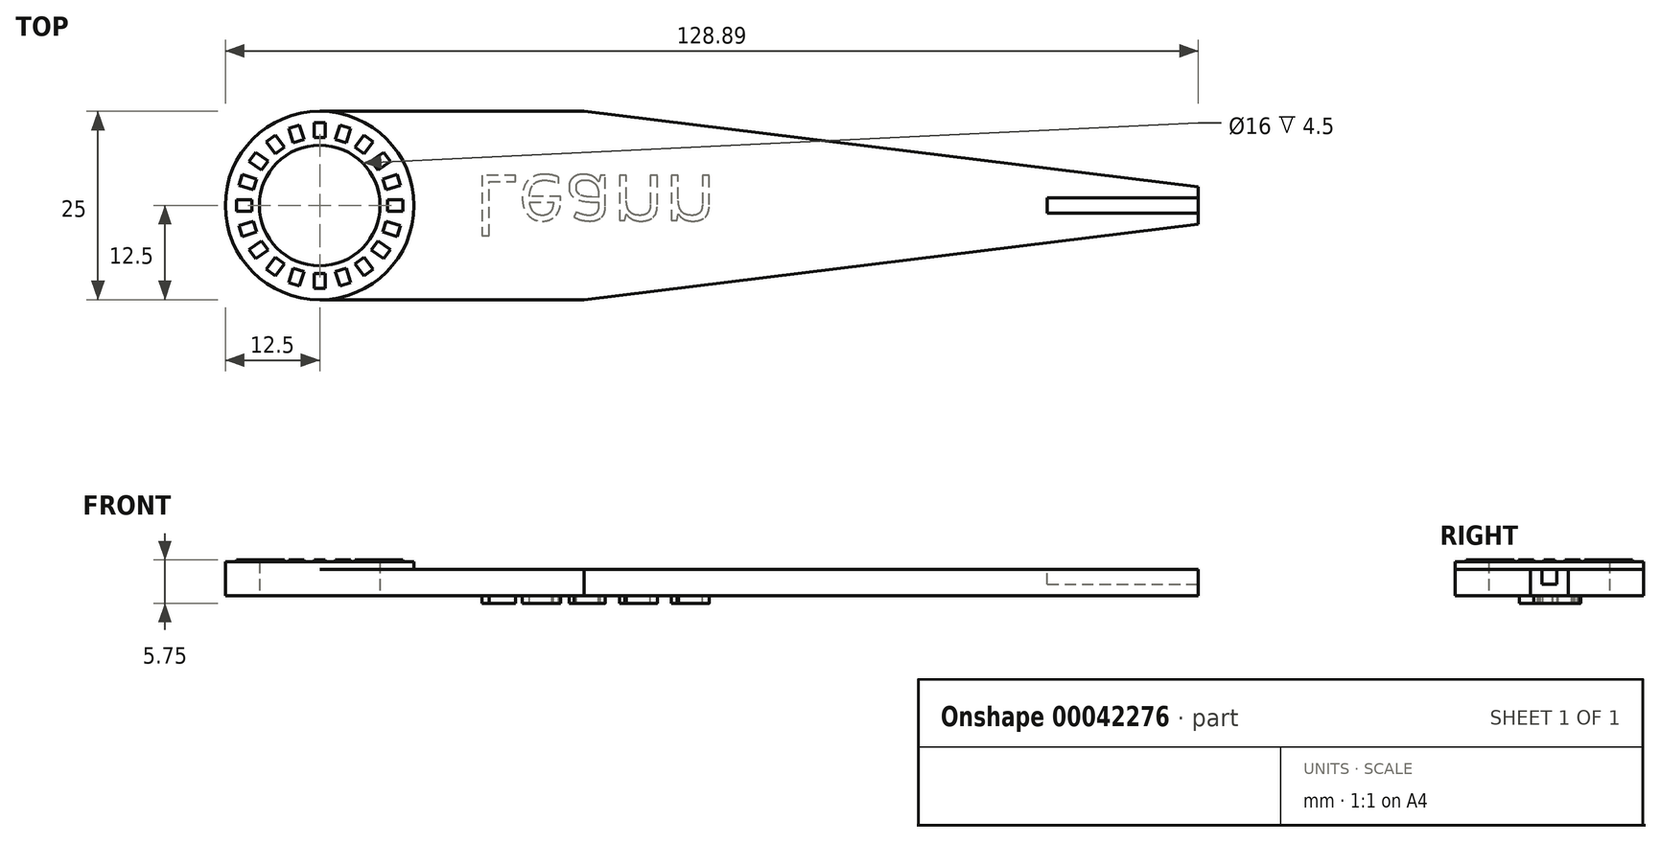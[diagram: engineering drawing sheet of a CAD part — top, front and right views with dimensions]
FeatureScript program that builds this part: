
annotation { "Feature Type Name" : "Feature", "Feature Type Description" : "" }
export const myFeature = defineFeature(function(context is Context, id is Id, definition is map)
    precondition{}
    {
        {
            var Q0;
            Q0=qCreatedBy(makeId("Top.planeOp"),FACE);
            var sketch = newSketch(context, id + "F0", { "sketchPlane" : qUnion([Q0])});
            skCircle(sketch, "E0", {"center": v(0, 0) * mm, "radius": 8 * mm});
            skArc(sketch, "E1", {"start": v(0, 12.5) * mm, "mid": v(-12.5, 0) * mm, "end": v(0, -12.5) * mm});
            skLineSegment(sketch, "E2", {"start": v(0, 12.5) * mm, "end": v(35, 12.5) * mm});
            skLineSegment(sketch, "E3", {"start": v(35, 12.5) * mm, "end": v(116.39, 2.5) * mm});
            skLineSegment(sketch, "E4", {"start": v(35, 12.5) * mm, "end": v(79.82, 12.5) * mm, "construction": true});
            skLineSegment(sketch, "E5", {"start": v(0, 0) * mm, "end": v(36.3, 0) * mm, "construction": true});
            skLineSegment(sketch, "E6.MirrorCS", {"start": v(0, -12.5) * mm, "end": v(35, -12.5) * mm});
            skLineSegment(sketch, "E7.MirrorCS", {"start": v(35, -12.5) * mm, "end": v(116.39, -2.5) * mm});
            skLineSegment(sketch, "E8", {"start": v(116.39, 2.5) * mm, "end": v(116.39, -2.5) * mm});
            skSolve(sketch);
        }
        {
            var Q0;
            Q0 = qSketchRegion(id + "F0", true);
            extrude(context, id + "F1", {"entities" : qUnion([Q0]), "depth" : 3.5 * mm});
        }
        {
            var Q0;
            Q0=makeQuery(id+"F1.opExtrude","CAP_FACE",FACE,{"disambiguationData":[OSD([sQuery(id+"F0.wireOp",EDGE,"E0"),sQuery(id+"F0.wireOp",EDGE,"E1"),sQuery(id+"F0.wireOp",EDGE,"E2"),sQuery(id+"F0.wireOp",EDGE,"E3"),sQuery(id+"F0.wireOp",EDGE,"E6.MirrorCS"),sQuery(id+"F0.wireOp",EDGE,"E7.MirrorCS"),sQuery(id+"F0.wireOp",EDGE,"E8")])],"isStart":false});
            var sketch = newSketch(context, id + "F2", { "sketchPlane" : qUnion([Q0])});
            skCircle(sketch, "E9", {"center": v(0, 0) * mm, "radius": 8 * mm});
            skCircle(sketch, "E10", {"center": v(0, 0) * mm, "radius": 12.5 * mm});
            skSolve(sketch);
        }
        {
            var Q0;
            Q0 = qSketchRegion(id + "F2", true);
            extrude(context, id + "F3", {"entities" : qUnion([Q0]), "operationType" : NewBodyOperationType.ADD, "depth" : 1 * mm});
        }
        {
            var Q0;
            Q0=makeQuery(id+"F3.opExtrude","CAP_FACE",FACE,{"disambiguationData":[OSD([sQuery(id+"F2.wireOp",EDGE,"E9"),sQuery(id+"F2.wireOp",EDGE,"E10")])],"isStart":false});
            var sketch = newSketch(context, id + "F4", { "sketchPlane" : qUnion([Q0])});
            skLineSegment(sketch, "E11.bottom", {"start": v(-0.75, 11) * mm, "end": v(0.75, 11) * mm});
            skLineSegment(sketch, "E11.top", {"start": v(-0.75, 9) * mm, "end": v(0.75, 9) * mm});
            skLineSegment(sketch, "E11.left", {"start": v(-0.75, 11) * mm, "end": v(-0.75, 9) * mm});
            skLineSegment(sketch, "E11.right", {"start": v(0.75, 11) * mm, "end": v(0.75, 9) * mm});
            skPoint(sketch, "E12", {"position": v(0, 8) * mm});
            skLineSegment(sketch, "E13.1.0", {"start": v(-4.11, 10.23) * mm, "end": v(-2.69, 10.7) * mm});
            skLineSegment(sketch, "E13.1.1", {"start": v(-4.11, 10.23) * mm, "end": v(-3.5, 8.33) * mm});
            skLineSegment(sketch, "E13.1.2", {"start": v(-3.5, 8.33) * mm, "end": v(-2.07, 8.8) * mm});
            skLineSegment(sketch, "E13.1.3", {"start": v(-2.69, 10.7) * mm, "end": v(-2.07, 8.8) * mm});
            skLineSegment(sketch, "E13.2.0", {"start": v(-7.07, 8.46) * mm, "end": v(-5.86, 9.34) * mm});
            skLineSegment(sketch, "E13.2.1", {"start": v(-7.07, 8.46) * mm, "end": v(-5.9, 6.84) * mm});
            skLineSegment(sketch, "E13.2.2", {"start": v(-5.9, 6.84) * mm, "end": v(-4.68, 7.72) * mm});
            skLineSegment(sketch, "E13.2.3", {"start": v(-5.86, 9.34) * mm, "end": v(-4.68, 7.72) * mm});
            skLineSegment(sketch, "E13.3.0", {"start": v(-9.34, 5.86) * mm, "end": v(-8.46, 7.07) * mm});
            skLineSegment(sketch, "E13.3.1", {"start": v(-9.34, 5.86) * mm, "end": v(-7.72, 4.68) * mm});
            skLineSegment(sketch, "E13.3.2", {"start": v(-7.72, 4.68) * mm, "end": v(-6.84, 5.9) * mm});
            skLineSegment(sketch, "E13.3.3", {"start": v(-8.46, 7.07) * mm, "end": v(-6.84, 5.9) * mm});
            skLineSegment(sketch, "E13.4.0", {"start": v(-10.7, 2.69) * mm, "end": v(-10.23, 4.11) * mm});
            skLineSegment(sketch, "E13.4.1", {"start": v(-10.7, 2.69) * mm, "end": v(-8.8, 2.07) * mm});
            skLineSegment(sketch, "E13.4.2", {"start": v(-8.8, 2.07) * mm, "end": v(-8.33, 3.5) * mm});
            skLineSegment(sketch, "E13.4.3", {"start": v(-10.23, 4.11) * mm, "end": v(-8.33, 3.5) * mm});
            skLineSegment(sketch, "E13.5.0", {"start": v(-11, -0.75) * mm, "end": v(-11, 0.75) * mm});
            skLineSegment(sketch, "E13.5.1", {"start": v(-11, -0.75) * mm, "end": v(-9, -0.75) * mm});
            skLineSegment(sketch, "E13.5.2", {"start": v(-9, -0.75) * mm, "end": v(-9, 0.75) * mm});
            skLineSegment(sketch, "E13.5.3", {"start": v(-11, 0.75) * mm, "end": v(-9, 0.75) * mm});
            skLineSegment(sketch, "E13.6.0", {"start": v(-10.23, -4.11) * mm, "end": v(-10.7, -2.69) * mm});
            skLineSegment(sketch, "E13.6.1", {"start": v(-10.23, -4.11) * mm, "end": v(-8.33, -3.5) * mm});
            skLineSegment(sketch, "E13.6.2", {"start": v(-8.33, -3.5) * mm, "end": v(-8.8, -2.07) * mm});
            skLineSegment(sketch, "E13.6.3", {"start": v(-10.7, -2.69) * mm, "end": v(-8.8, -2.07) * mm});
            skLineSegment(sketch, "E13.7.0", {"start": v(-8.46, -7.07) * mm, "end": v(-9.34, -5.86) * mm});
            skLineSegment(sketch, "E13.7.1", {"start": v(-8.46, -7.07) * mm, "end": v(-6.84, -5.9) * mm});
            skLineSegment(sketch, "E13.7.2", {"start": v(-6.84, -5.9) * mm, "end": v(-7.72, -4.68) * mm});
            skLineSegment(sketch, "E13.7.3", {"start": v(-9.34, -5.86) * mm, "end": v(-7.72, -4.68) * mm});
            skLineSegment(sketch, "E13.8.0", {"start": v(-5.86, -9.34) * mm, "end": v(-7.07, -8.46) * mm});
            skLineSegment(sketch, "E13.8.1", {"start": v(-5.86, -9.34) * mm, "end": v(-4.68, -7.72) * mm});
            skLineSegment(sketch, "E13.8.2", {"start": v(-4.68, -7.72) * mm, "end": v(-5.9, -6.84) * mm});
            skLineSegment(sketch, "E13.8.3", {"start": v(-7.07, -8.46) * mm, "end": v(-5.9, -6.84) * mm});
            skLineSegment(sketch, "E13.9.0", {"start": v(-2.69, -10.7) * mm, "end": v(-4.11, -10.23) * mm});
            skLineSegment(sketch, "E13.9.1", {"start": v(-2.69, -10.7) * mm, "end": v(-2.07, -8.8) * mm});
            skLineSegment(sketch, "E13.9.2", {"start": v(-2.07, -8.8) * mm, "end": v(-3.5, -8.33) * mm});
            skLineSegment(sketch, "E13.9.3", {"start": v(-4.11, -10.23) * mm, "end": v(-3.5, -8.33) * mm});
            skLineSegment(sketch, "E13.10.0", {"start": v(0.75, -11) * mm, "end": v(-0.75, -11) * mm});
            skLineSegment(sketch, "E13.10.1", {"start": v(0.75, -11) * mm, "end": v(0.75, -9) * mm});
            skLineSegment(sketch, "E13.10.2", {"start": v(0.75, -9) * mm, "end": v(-0.75, -9) * mm});
            skLineSegment(sketch, "E13.10.3", {"start": v(-0.75, -11) * mm, "end": v(-0.75, -9) * mm});
            skLineSegment(sketch, "E13.11.0", {"start": v(4.11, -10.23) * mm, "end": v(2.69, -10.7) * mm});
            skLineSegment(sketch, "E13.11.1", {"start": v(4.11, -10.23) * mm, "end": v(3.5, -8.33) * mm});
            skLineSegment(sketch, "E13.11.2", {"start": v(3.5, -8.33) * mm, "end": v(2.07, -8.8) * mm});
            skLineSegment(sketch, "E13.11.3", {"start": v(2.69, -10.7) * mm, "end": v(2.07, -8.8) * mm});
            skLineSegment(sketch, "E13.12.0", {"start": v(7.07, -8.46) * mm, "end": v(5.86, -9.34) * mm});
            skLineSegment(sketch, "E13.12.1", {"start": v(7.07, -8.46) * mm, "end": v(5.9, -6.84) * mm});
            skLineSegment(sketch, "E13.12.2", {"start": v(5.9, -6.84) * mm, "end": v(4.68, -7.72) * mm});
            skLineSegment(sketch, "E13.12.3", {"start": v(5.86, -9.34) * mm, "end": v(4.68, -7.72) * mm});
            skLineSegment(sketch, "E13.13.0", {"start": v(9.34, -5.86) * mm, "end": v(8.46, -7.07) * mm});
            skLineSegment(sketch, "E13.13.1", {"start": v(9.34, -5.86) * mm, "end": v(7.72, -4.68) * mm});
            skLineSegment(sketch, "E13.13.2", {"start": v(7.72, -4.68) * mm, "end": v(6.84, -5.9) * mm});
            skLineSegment(sketch, "E13.13.3", {"start": v(8.46, -7.07) * mm, "end": v(6.84, -5.9) * mm});
            skLineSegment(sketch, "E13.14.0", {"start": v(10.7, -2.69) * mm, "end": v(10.23, -4.11) * mm});
            skLineSegment(sketch, "E13.14.1", {"start": v(10.7, -2.69) * mm, "end": v(8.8, -2.07) * mm});
            skLineSegment(sketch, "E13.14.2", {"start": v(8.8, -2.07) * mm, "end": v(8.33, -3.5) * mm});
            skLineSegment(sketch, "E13.14.3", {"start": v(10.23, -4.11) * mm, "end": v(8.33, -3.5) * mm});
            skLineSegment(sketch, "E13.15.0", {"start": v(11, 0.75) * mm, "end": v(11, -0.75) * mm});
            skLineSegment(sketch, "E13.15.1", {"start": v(11, 0.75) * mm, "end": v(9, 0.75) * mm});
            skLineSegment(sketch, "E13.15.2", {"start": v(9, 0.75) * mm, "end": v(9, -0.75) * mm});
            skLineSegment(sketch, "E13.15.3", {"start": v(11, -0.75) * mm, "end": v(9, -0.75) * mm});
            skLineSegment(sketch, "E13.16.0", {"start": v(10.23, 4.11) * mm, "end": v(10.7, 2.69) * mm});
            skLineSegment(sketch, "E13.16.1", {"start": v(10.23, 4.11) * mm, "end": v(8.33, 3.5) * mm});
            skLineSegment(sketch, "E13.16.2", {"start": v(8.33, 3.5) * mm, "end": v(8.8, 2.07) * mm});
            skLineSegment(sketch, "E13.16.3", {"start": v(10.7, 2.69) * mm, "end": v(8.8, 2.07) * mm});
            skLineSegment(sketch, "E13.17.0", {"start": v(8.46, 7.07) * mm, "end": v(9.34, 5.86) * mm});
            skLineSegment(sketch, "E13.17.1", {"start": v(8.46, 7.07) * mm, "end": v(6.84, 5.9) * mm});
            skLineSegment(sketch, "E13.17.2", {"start": v(6.84, 5.9) * mm, "end": v(7.72, 4.68) * mm});
            skLineSegment(sketch, "E13.17.3", {"start": v(9.34, 5.86) * mm, "end": v(7.72, 4.68) * mm});
            skLineSegment(sketch, "E13.18.0", {"start": v(5.86, 9.34) * mm, "end": v(7.07, 8.46) * mm});
            skLineSegment(sketch, "E13.18.1", {"start": v(5.86, 9.34) * mm, "end": v(4.68, 7.72) * mm});
            skLineSegment(sketch, "E13.18.2", {"start": v(4.68, 7.72) * mm, "end": v(5.9, 6.84) * mm});
            skLineSegment(sketch, "E13.18.3", {"start": v(7.07, 8.46) * mm, "end": v(5.9, 6.84) * mm});
            skLineSegment(sketch, "E13.19.0", {"start": v(2.69, 10.7) * mm, "end": v(4.11, 10.23) * mm});
            skLineSegment(sketch, "E13.19.1", {"start": v(2.69, 10.7) * mm, "end": v(2.07, 8.8) * mm});
            skLineSegment(sketch, "E13.19.2", {"start": v(2.07, 8.8) * mm, "end": v(3.5, 8.33) * mm});
            skLineSegment(sketch, "E13.19.3", {"start": v(4.11, 10.23) * mm, "end": v(3.5, 8.33) * mm});
            skPoint(sketch, "E13.center", {"position": v(0, 0) * mm});
            skSolve(sketch);
        }
        {
            var Q0;
            Q0 = qSketchRegion(id + "F4", true);
            extrude(context, id + "F5", {"entities" : qUnion([Q0]), "operationType" : NewBodyOperationType.ADD, "depth" : .25 * mm});
        }
        {
            var Q0;
            Q0=makeQuery(id+"F1.opExtrude","CAP_FACE",FACE,{"disambiguationData":[OSD([sQuery(id+"F0.wireOp",EDGE,"E0"),sQuery(id+"F0.wireOp",EDGE,"E1"),sQuery(id+"F0.wireOp",EDGE,"E2"),sQuery(id+"F0.wireOp",EDGE,"E3"),sQuery(id+"F0.wireOp",EDGE,"E6.MirrorCS"),sQuery(id+"F0.wireOp",EDGE,"E7.MirrorCS"),sQuery(id+"F0.wireOp",EDGE,"E8")])],"isStart":false});
            var sketch = newSketch(context, id + "F6", { "sketchPlane" : qUnion([Q0])});
            skLineSegment(sketch, "E14.bottom", {"start": v(96.39, 1) * mm, "end": v(116.39, 1) * mm});
            skLineSegment(sketch, "E14.top", {"start": v(96.39, -1) * mm, "end": v(116.39, -1) * mm});
            skLineSegment(sketch, "E14.left", {"start": v(96.39, 1) * mm, "end": v(96.39, -1) * mm});
            skLineSegment(sketch, "E14.right", {"start": v(116.39, 1) * mm, "end": v(116.39, -1) * mm});
            skSolve(sketch);
        }
        {
            var Q0;
            Q0 = qSketchRegion(id + "F6", true);
            extrude(context, id + "F7", {"entities" : qUnion([Q0]), "operationType" : NewBodyOperationType.REMOVE, "oppositeDirection" : true, "depth" : 2 * mm});
        }
        {
            var Q0;
            Q0=makeQuery(id+"F1.opExtrude","CAP_FACE",FACE,{"disambiguationData":[OSD([sQuery(id+"F0.wireOp",EDGE,"E0"),sQuery(id+"F0.wireOp",EDGE,"E1"),sQuery(id+"F0.wireOp",EDGE,"E2"),sQuery(id+"F0.wireOp",EDGE,"E3"),sQuery(id+"F0.wireOp",EDGE,"E6.MirrorCS"),sQuery(id+"F0.wireOp",EDGE,"E7.MirrorCS"),sQuery(id+"F0.wireOp",EDGE,"E8")])],"isStart":true});
            var sketch = newSketch(context, id + "F8", { "sketchPlane" : qUnion([Q0])});
            skText(sketch, "E15", { "text": "Leann", "fontName": "OpenSans-Regular.ttf"});
            const initialGuessF8  = {"E15": [0.0204, -0.00403, 1, 0, 0.00807]};
            skSetInitialGuess(sketch, initialGuessF8);
            skSolve(sketch);
        }
        {
            var Q0;
            Q0 = qSketchRegion(id + "F8", true);
            extrude(context, id + "F9", {"entities" : qUnion([Q0]), "operationType" : NewBodyOperationType.ADD, "depth" : 1 * mm});
        }
    });
